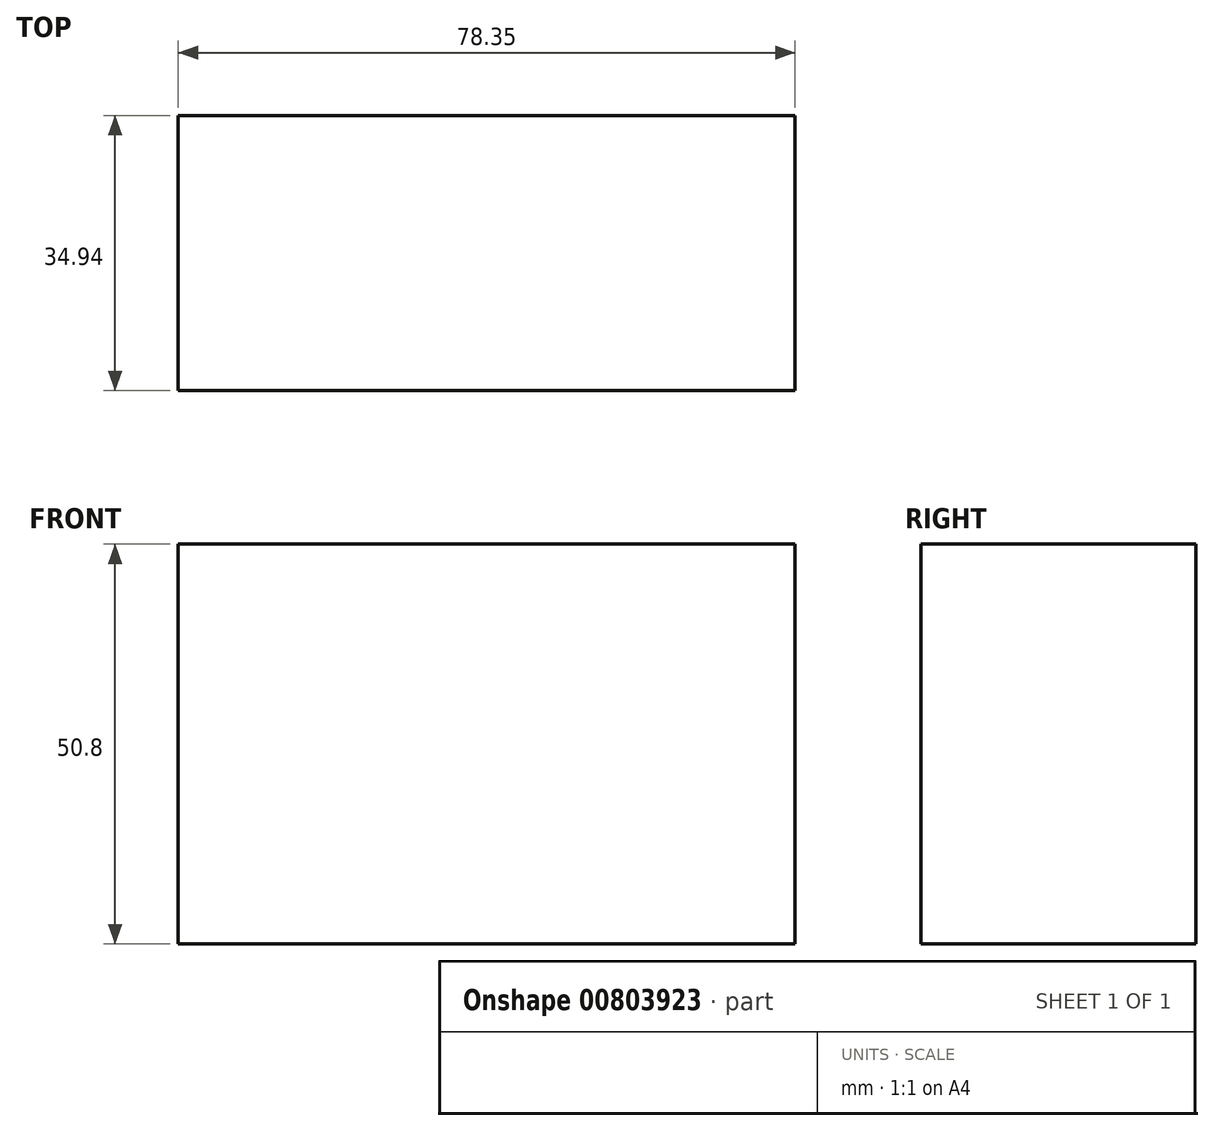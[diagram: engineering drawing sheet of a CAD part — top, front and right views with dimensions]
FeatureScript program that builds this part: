
annotation { "Feature Type Name" : "Feature", "Feature Type Description" : "" }
export const myFeature = defineFeature(function(context is Context, id is Id, definition is map)
    precondition{}
    {
        {
            var Q0;
            Q0=qCreatedBy(makeId("Top.planeOp"),FACE);
            var sketch = newSketch(context, id + "F0", { "sketchPlane" : qUnion([Q0])});
            skLineSegment(sketch, "E0.bottom", {"start": v(-37.26, 16.79) * mm, "end": v(41.09, 16.79) * mm});
            skLineSegment(sketch, "E0.top", {"start": v(-37.26, -18.15) * mm, "end": v(41.09, -18.15) * mm});
            skLineSegment(sketch, "E0.left", {"start": v(-37.26, 16.79) * mm, "end": v(-37.26, -18.15) * mm});
            skLineSegment(sketch, "E0.right", {"start": v(41.09, 16.79) * mm, "end": v(41.09, -18.15) * mm});
            skSolve(sketch);
        }
        {
            var Q0;
            Q0=makeQuery(id+"F0.imprint","IMPRINT",FACE,{"disambiguationData":[TD([[makeQuery(id+"F0.imprint","IMPRINT",EDGE,{"derivedFrom":sQuery(id+"F0.wireOp",EDGE,"E0.bottom")}),-1.0]])]});
            extrude(context, id + "F1", {"entities" : qUnion([Q0]), "depth" : 50.8 * mm, "offsetDistance" : 25.4 * mm});
        }
    });
